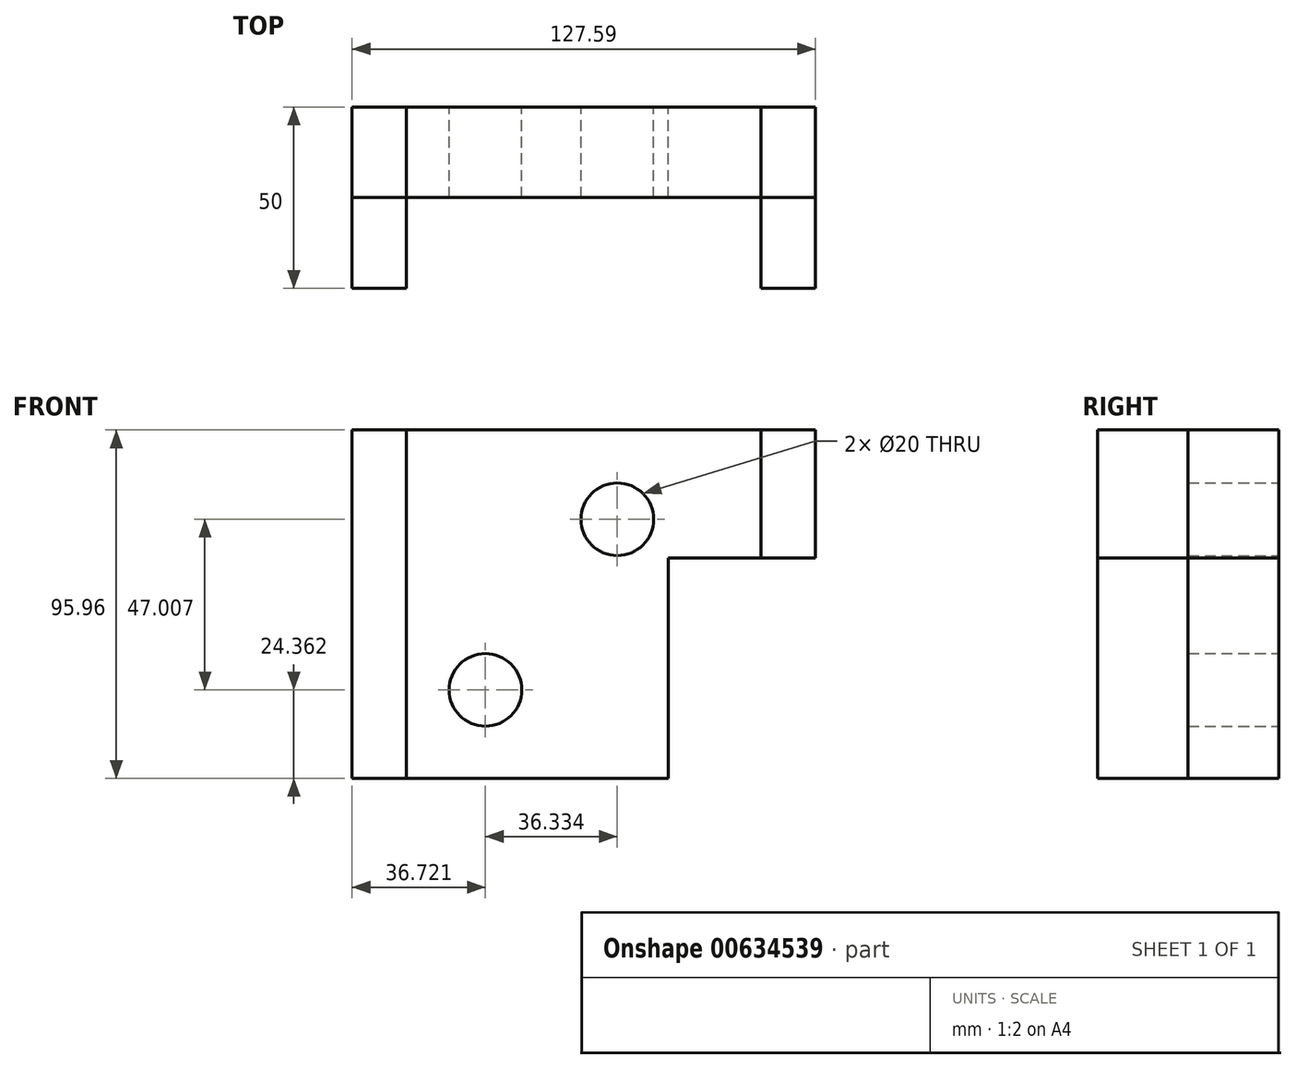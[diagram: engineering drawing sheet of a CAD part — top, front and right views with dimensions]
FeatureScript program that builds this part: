
annotation { "Feature Type Name" : "Feature", "Feature Type Description" : "" }
export const myFeature = defineFeature(function(context is Context, id is Id, definition is map)
    precondition{}
    {
        {
            var Q0;
            Q0=qCreatedBy(makeId("Front.planeOp"),FACE);
            var sketch = newSketch(context, id + "F0", { "sketchPlane" : qUnion([Q0])});
            skLineSegment(sketch, "E0", {"start": v(-60.36, 45.08) * mm, "end": v(-60.36, -50.88) * mm});
            skLineSegment(sketch, "E1", {"start": v(-60.36, -50.88) * mm, "end": v(26.78, -50.88) * mm});
            skLineSegment(sketch, "E2", {"start": v(26.78, -50.88) * mm, "end": v(26.78, 9.8) * mm});
            skLineSegment(sketch, "E3", {"start": v(26.78, 9.8) * mm, "end": v(67.23, 9.8) * mm});
            skLineSegment(sketch, "E4", {"start": v(67.23, 9.8) * mm, "end": v(67.23, 45.08) * mm});
            skLineSegment(sketch, "E5", {"start": v(67.23, 45.08) * mm, "end": v(-60.36, 45.08) * mm});
            skPoint(sketch, "E6.orphan", {"position": v(-60.36, 47.45) * mm});
            skLineSegment(sketch, "E7", {"start": v(-45.36, 45.08) * mm, "end": v(-45.36, -50.88) * mm});
            skLineSegment(sketch, "E8", {"start": v(52.23, 45.08) * mm, "end": v(52.23, 9.8) * mm});
            skCircle(sketch, "E9", {"center": v(-23.64, -26.52) * mm, "radius": 10 * mm});
            skCircle(sketch, "E10", {"center": v(12.7, 20.49) * mm, "radius": 10 * mm});
            skSolve(sketch);
        }
        {
            var Q0;
            {var subQ0=sQuery(id+"F0.wireOp",EDGE,"E0");Q0=makeQuery(id+"F0.imprint","IMPRINT",FACE,{"disambiguationData":[TD([[makeQuery(id+"F0.imprint","IMPRINT",EDGE,{"derivedFrom":subQ0}),1.0]])]});}
            var Q1;
            {var subQ0=sQuery(id+"F0.wireOp",EDGE,"E4");Q1=makeQuery(id+"F0.imprint","IMPRINT",FACE,{"disambiguationData":[TD([[makeQuery(id+"F0.imprint","IMPRINT",EDGE,{"derivedFrom":subQ0}),1.0]])]});}
            extrude(context, id + "F1", {"entities" : qUnion([Q0, Q1]), "depth" : 50 * mm, "offsetDistance" : 25 * mm});
        }
        {
            var Q0;
            Q0 = qSketchRegion(id + "F0", true);
            extrude(context, id + "F2", {"entities" : qUnion([Q0]), "depth" : 25 * mm, "offsetDistance" : 25 * mm});
        }
    });
